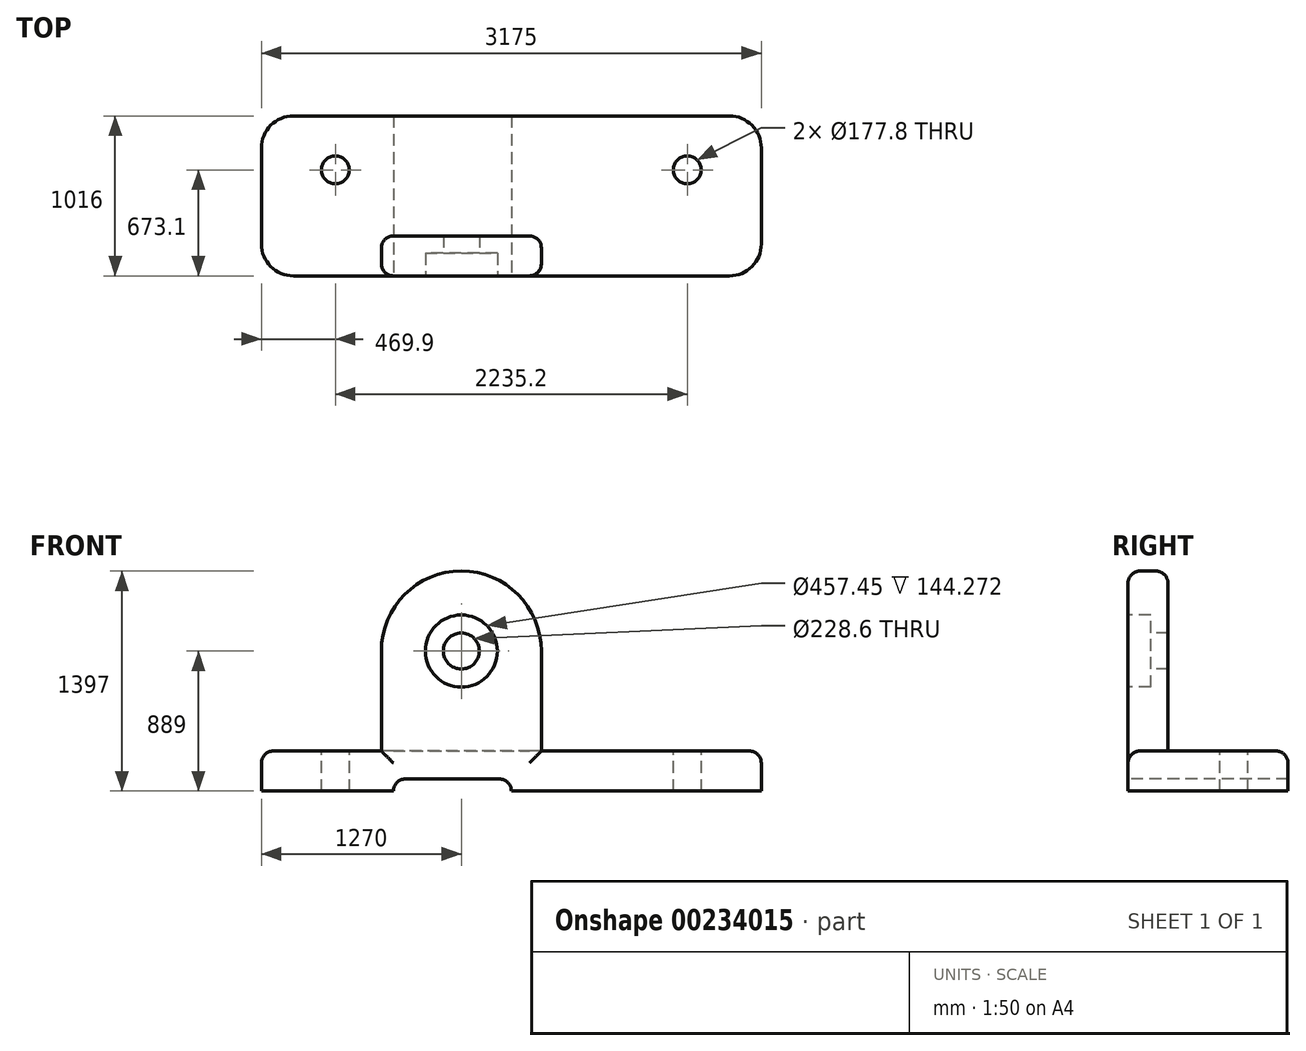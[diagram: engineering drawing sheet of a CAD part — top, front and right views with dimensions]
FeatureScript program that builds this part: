
annotation { "Feature Type Name" : "Feature", "Feature Type Description" : "" }
export const myFeature = defineFeature(function(context is Context, id is Id, definition is map)
    precondition{}
    {
        {
            var Q0;
            Q0=qCreatedBy(makeId("Top.planeOp"),FACE);
            var sketch = newSketch(context, id + "F0", { "sketchPlane" : qUnion([Q0])});
            skLineSegment(sketch, "E0.bottom", {"start": v(1587.5, -508) * mm, "end": v(-1587.5, -508) * mm});
            skLineSegment(sketch, "E0.top", {"start": v(1587.5, 508) * mm, "end": v(-1587.5, 508) * mm});
            skLineSegment(sketch, "E0.left", {"start": v(1587.5, -508) * mm, "end": v(1587.5, 508) * mm});
            skLineSegment(sketch, "E0.right", {"start": v(-1587.5, -508) * mm, "end": v(-1587.5, 508) * mm});
            skPoint(sketch, "E0.middle", {"position": v(0, 0) * mm});
            skSolve(sketch);
        }
        {
            var Q0;
            Q0=makeQuery(id+"F0.imprint","IMPRINT",FACE,{"disambiguationData":[TD([[makeQuery(id+"F0.imprint","IMPRINT",EDGE,{"derivedFrom":sQuery(id+"F0.wireOp",EDGE,"E0.bottom")}),-1.0]])]});
            extrude(context, id + "F1", {"entities" : qUnion([Q0]), "depth" : 254 * mm});
        }
        {
            var Q0;
            Q0=makeQuery(id+"F1.opExtrude","CAP_FACE",FACE,{"disambiguationData":[OSD([sQuery(id+"F0.wireOp",EDGE,"E0.bottom"),sQuery(id+"F0.wireOp",EDGE,"E0.top"),sQuery(id+"F0.wireOp",EDGE,"E0.left"),sQuery(id+"F0.wireOp",EDGE,"E0.right")])],"isStart":false});
            var sketch = newSketch(context, id + "F2", { "sketchPlane" : qUnion([Q0])});
            skLineSegment(sketch, "E1.bottom", {"start": v(-825.5, -508) * mm, "end": v(190.5, -508) * mm});
            skLineSegment(sketch, "E1.top", {"start": v(-825.5, -254) * mm, "end": v(190.5, -254) * mm});
            skLineSegment(sketch, "E1.left", {"start": v(-825.5, -508) * mm, "end": v(-825.5, -254) * mm});
            skLineSegment(sketch, "E1.right", {"start": v(190.5, -508) * mm, "end": v(190.5, -254) * mm});
            skSolve(sketch);
        }
        {
            var Q0;
            Q0=makeQuery(id+"F2.imprint","IMPRINT",FACE,{"disambiguationData":[TD([[makeQuery(id+"F2.imprint","IMPRINT",EDGE,{"derivedFrom":sQuery(id+"F2.wireOp",EDGE,"E1.bottom")}),-1.0]])]});
            extrude(context, id + "F3", {"entities" : qUnion([Q0]), "operationType" : NewBodyOperationType.ADD, "depth" : 1143 * mm});
        }
        {
            var Q0;
            Q0=makeQuery(id+"F3.opExtrude","CAP_EDGE",EDGE,{"disambiguationData":[OSD([sQuery(id+"F2.wireOp",EDGE,"E1.right")])],"isStart":false});
            var Q1;
            Q1=makeQuery(id+"F3.opExtrude","CAP_EDGE",EDGE,{"disambiguationData":[OSD([sQuery(id+"F2.wireOp",EDGE,"E1.left")])],"isStart":false});
            fillet(context, id + "F4", {"entities" : qUnion([Q0, Q1]), "radius" : 508 * mm, "tangentPropagation" : true, "allowEdgeOverflow" : false});
        }
        {
            var Q0;
            Q0=makeQuery(id+"F4.opFillet","BLEND_EDGE",EDGE,{"blendedFrom":[makeQuery(id+"F3.opExtrude","CAP_EDGE",EDGE,{"disambiguationData":[OSD([sQuery(id+"F2.wireOp",EDGE,"E1.left")])],"isStart":false}),makeQuery(id+"F3.boolean.opBoolean","MERGE",FACE,{"derivedFrom":[makeQuery(id+"F1.opExtrude","SWEPT_FACE",FACE,{"disambiguationData":[OSD([sQuery(id+"F0.wireOp",EDGE,"E0.bottom")])]}),makeQuery(id+"F3.opExtrude","SWEPT_FACE",FACE,{"disambiguationData":[OSD([sQuery(id+"F2.wireOp",EDGE,"E1.bottom")])]})]})],"blendedInto":[makeQuery(id+"F3.boolean.opBoolean","MERGE",FACE,{"derivedFrom":[makeQuery(id+"F1.opExtrude","SWEPT_FACE",FACE,{"disambiguationData":[OSD([sQuery(id+"F0.wireOp",EDGE,"E0.bottom")])]}),makeQuery(id+"F3.opExtrude","SWEPT_FACE",FACE,{"disambiguationData":[OSD([sQuery(id+"F2.wireOp",EDGE,"E1.bottom")])]})]})]});
            var Q1;
            {var subQ0=sQuery(id+"F0.wireOp",EDGE,"E0.left");var subQ1=sQuery(id+"F0.wireOp",EDGE,"E0.bottom");Q1=makeQuery(id+"F3.boolean.opBoolean","SPLIT",EDGE,{"disambiguationData":[TD([makeQuery(id+"F1.opExtrude","SWEPT_FACE",FACE,{"disambiguationData":[OSD([subQ0])]})])],"derivedFrom":makeQuery(id+"F1.opExtrude","CAP_EDGE",EDGE,{"disambiguationData":[OSD([subQ1])],"isStart":false})});}
            var Q2;
            {var subQ0=sQuery(id+"F0.wireOp",EDGE,"E0.right");var subQ1=sQuery(id+"F0.wireOp",EDGE,"E0.bottom");Q2=makeQuery(id+"F3.boolean.opBoolean","SPLIT",EDGE,{"disambiguationData":[TD([makeQuery(id+"F1.opExtrude","SWEPT_FACE",FACE,{"disambiguationData":[OSD([subQ0])]})])],"derivedFrom":makeQuery(id+"F1.opExtrude","CAP_EDGE",EDGE,{"disambiguationData":[OSD([subQ1])],"isStart":false})});}
            var Q3;
            Q3=makeQuery(id+"F1.opExtrude","CAP_EDGE",EDGE,{"disambiguationData":[OSD([sQuery(id+"F0.wireOp",EDGE,"E0.top")])],"isStart":false});
            var Q4;
            Q4=makeQuery(id+"F1.opExtrude","CAP_EDGE",EDGE,{"disambiguationData":[OSD([sQuery(id+"F0.wireOp",EDGE,"E0.left")])],"isStart":false});
            var Q5;
            Q5=makeQuery(id+"F1.opExtrude","CAP_EDGE",EDGE,{"disambiguationData":[OSD([sQuery(id+"F0.wireOp",EDGE,"E0.right")])],"isStart":false});
            var Q6;
            Q6=makeQuery(id+"F4.opFillet","BLEND_EDGE",EDGE,{"blendedFrom":[makeQuery(id+"F3.opExtrude","CAP_EDGE",EDGE,{"disambiguationData":[OSD([sQuery(id+"F2.wireOp",EDGE,"E1.left")])],"isStart":false}),makeQuery(id+"F3.opExtrude","SWEPT_FACE",FACE,{"disambiguationData":[OSD([sQuery(id+"F2.wireOp",EDGE,"E1.top")])]})],"blendedInto":[makeQuery(id+"F3.opExtrude","SWEPT_FACE",FACE,{"disambiguationData":[OSD([sQuery(id+"F2.wireOp",EDGE,"E1.top")])]})]});
            var Q7;
            Q7=makeQuery(id+"F3.opExtrude","CAP_EDGE",EDGE,{"disambiguationData":[OSD([sQuery(id+"F2.wireOp",EDGE,"E1.right")])],"isStart":true});
            fillet(context, id + "F5", {"entities" : qUnion([Q0, Q1, Q2, Q3, Q4, Q5, Q6, Q7]), "radius" : 76.2 * mm, "tangentPropagation" : true, "allowEdgeOverflow" : false});
        }
        {
            var Q0;
            Q0=makeQuery(id+"F3.boolean.opBoolean","MERGE",FACE,{"derivedFrom":[makeQuery(id+"F1.opExtrude","SWEPT_FACE",FACE,{"disambiguationData":[OSD([sQuery(id+"F0.wireOp",EDGE,"E0.bottom")])]}),makeQuery(id+"F3.opExtrude","SWEPT_FACE",FACE,{"disambiguationData":[OSD([sQuery(id+"F2.wireOp",EDGE,"E1.bottom")])]})]});
            var sketch = newSketch(context, id + "F6", { "sketchPlane" : qUnion([Q0])});
            skCircle(sketch, "E2", {"center": v(-317.5, 889) * mm, "radius": 228.73 * mm});
            skCircle(sketch, "E3", {"center": v(-317.5, 889) * mm, "radius": 114.3 * mm});
            skSolve(sketch);
        }
        {
            var Q0;
            Q0=makeQuery(id+"F6.imprint","IMPRINT",FACE,{"disambiguationData":[TD([[makeQuery(id+"F6.imprint","IMPRINT",EDGE,{"derivedFrom":sQuery(id+"F6.wireOp",EDGE,"E2")}),1.0]])]});
            extrude(context, id + "F7", {"entities" : qUnion([Q0]), "operationType" : NewBodyOperationType.REMOVE, "oppositeDirection" : true, "depth" : 144.27 * mm});
        }
        {
            var Q0;
            Q0=makeQuery(id+"F7.boolean.opBoolean","SPLIT",FACE,{"disambiguationData":[TD([makeQuery(id+"F7.opExtrude","SWEPT_FACE",FACE,{"disambiguationData":[OSD([sQuery(id+"F6.wireOp",EDGE,"E3")])]})])],"derivedFrom":makeQuery(id+"F3.boolean.opBoolean","MERGE",FACE,{"derivedFrom":[makeQuery(id+"F1.opExtrude","SWEPT_FACE",FACE,{"disambiguationData":[OSD([sQuery(id+"F0.wireOp",EDGE,"E0.bottom")])]}),makeQuery(id+"F3.opExtrude","SWEPT_FACE",FACE,{"disambiguationData":[OSD([sQuery(id+"F2.wireOp",EDGE,"E1.bottom")])]})]})});
            extrude(context, id + "F8", {"entities" : qUnion([Q0]), "operationType" : NewBodyOperationType.REMOVE, "oppositeDirection" : true, "depth" : 817.88 * mm});
        }
        {
            var Q0;
            {var subQ0=sQuery(id+"F0.wireOp",EDGE,"E0.left");var subQ1=sQuery(id+"F0.wireOp",EDGE,"E0.bottom");Q0=makeQuery(id+"F5.opFillet","BLEND_EDGE",EDGE,{"blendedFrom":[makeQuery(id+"F1.opExtrude","CAP_EDGE",EDGE,{"disambiguationData":[OSD([subQ0])],"isStart":false}),makeQuery(id+"F3.boolean.opBoolean","SPLIT",EDGE,{"disambiguationData":[TD([makeQuery(id+"F1.opExtrude","SWEPT_FACE",FACE,{"disambiguationData":[OSD([subQ0])]})])],"derivedFrom":makeQuery(id+"F1.opExtrude","CAP_EDGE",EDGE,{"disambiguationData":[OSD([subQ1])],"isStart":false})})],"blendedInto":[]});}
            var Q1;
            Q1=makeQuery(id+"F5.opFillet","BLEND_EDGE",EDGE,{"blendedFrom":[makeQuery(id+"F1.opExtrude","CAP_EDGE",EDGE,{"disambiguationData":[OSD([sQuery(id+"F0.wireOp",EDGE,"E0.top")])],"isStart":false}),makeQuery(id+"F1.opExtrude","CAP_EDGE",EDGE,{"disambiguationData":[OSD([sQuery(id+"F0.wireOp",EDGE,"E0.left")])],"isStart":false})],"blendedInto":[]});
            var Q2;
            {var subQ0=sQuery(id+"F0.wireOp",EDGE,"E0.right");var subQ1=sQuery(id+"F0.wireOp",EDGE,"E0.bottom");Q2=makeQuery(id+"F5.opFillet","BLEND_EDGE",EDGE,{"blendedFrom":[makeQuery(id+"F1.opExtrude","CAP_EDGE",EDGE,{"disambiguationData":[OSD([subQ0])],"isStart":false}),makeQuery(id+"F3.boolean.opBoolean","SPLIT",EDGE,{"disambiguationData":[TD([makeQuery(id+"F1.opExtrude","SWEPT_FACE",FACE,{"disambiguationData":[OSD([subQ0])]})])],"derivedFrom":makeQuery(id+"F1.opExtrude","CAP_EDGE",EDGE,{"disambiguationData":[OSD([subQ1])],"isStart":false})})],"blendedInto":[]});}
            var Q3;
            Q3=makeQuery(id+"F5.opFillet","BLEND_EDGE",EDGE,{"blendedFrom":[makeQuery(id+"F1.opExtrude","CAP_EDGE",EDGE,{"disambiguationData":[OSD([sQuery(id+"F0.wireOp",EDGE,"E0.top")])],"isStart":false}),makeQuery(id+"F1.opExtrude","CAP_EDGE",EDGE,{"disambiguationData":[OSD([sQuery(id+"F0.wireOp",EDGE,"E0.right")])],"isStart":false})],"blendedInto":[]});
            fillet(context, id + "F9", {"entities" : qUnion([Q0, Q1, Q2, Q3]), "radius" : 203.2 * mm, "tangentPropagation" : true, "allowEdgeOverflow" : false});
        }
        {
            var Q0;
            Q0=makeQuery(id+"F1.opExtrude","CAP_FACE",FACE,{"disambiguationData":[OSD([sQuery(id+"F0.wireOp",EDGE,"E0.bottom"),sQuery(id+"F0.wireOp",EDGE,"E0.top"),sQuery(id+"F0.wireOp",EDGE,"E0.left"),sQuery(id+"F0.wireOp",EDGE,"E0.right")])],"isStart":false});
            var sketch = newSketch(context, id + "F10", { "sketchPlane" : qUnion([Q0])});
            skCircle(sketch, "E4", {"center": v(1117.6, 165.1) * mm, "radius": 88.9 * mm});
            skCircle(sketch, "E5", {"center": v(-1117.6, 165.1) * mm, "radius": 88.9 * mm});
            skSolve(sketch);
        }
        {
            var Q0;
            Q0 = qSketchRegion(id + "F10", true);
            extrude(context, id + "F11", {"entities" : qUnion([Q0]), "operationType" : NewBodyOperationType.REMOVE, "oppositeDirection" : true, "depth" : 792.48 * mm});
        }
        {
            var Q0;
            {var subQ2=sQuery(id+"F2.wireOp",EDGE,"E1.bottom");var subQ3=makeQuery(id+"F3.opExtrude","SWEPT_FACE",FACE,{"disambiguationData":[OSD([subQ2])]});var subQ4=sQuery(id+"F0.wireOp",EDGE,"E0.left");var subQ6=sQuery(id+"F0.wireOp",EDGE,"E0.bottom");var subQ8=makeQuery(id+"F1.opExtrude","SWEPT_FACE",FACE,{"disambiguationData":[OSD([subQ6])]});var subQ11=makeQuery(id+"F1.opExtrude","SWEPT_FACE",FACE,{"disambiguationData":[OSD([subQ4])]});var subQ13=makeQuery(id+"F3.boolean.opBoolean","MERGE",FACE,{"derivedFrom":[subQ8,subQ3]});Q0=makeQuery(id+"F7.boolean.opBoolean","SPLIT",FACE,{"disambiguationData":[TD([subQ11])],"derivedFrom":subQ13});}
            var sketch = newSketch(context, id + "F12", { "sketchPlane" : qUnion([Q0])});
            skLineSegment(sketch, "E6", {"start": v(-749.3, 0) * mm, "end": v(-749.3, 0) * mm});
            skLineSegment(sketch, "E7", {"start": v(-673.1, 76.2) * mm, "end": v(-76.2, 76.2) * mm});
            skLineSegment(sketch, "E8", {"start": v(0, 0) * mm, "end": v(0, 0) * mm});
            skLineSegment(sketch, "E9", {"start": v(0, 0) * mm, "end": v(-749.3, 0) * mm});
            skPoint(sketch, "E10.visualSharp", {"position": v(0, 76.2) * mm});
            skArc(sketch, "E10.filletArc", {"start": v(0, 0) * mm, "mid": v(-22.32, 53.88) * mm, "end": v(-76.2, 76.2) * mm});
            skPoint(sketch, "E11.visualSharp", {"position": v(-749.3, 76.2) * mm});
            skArc(sketch, "E11.filletArc", {"start": v(-673.1, 76.2) * mm, "mid": v(-726.98, 53.88) * mm, "end": v(-749.3, 0) * mm});
            skSolve(sketch);
        }
        {
            var Q0;
            Q0=makeQuery(id+"F12.imprint","IMPRINT",FACE,{"disambiguationData":[TD([[makeQuery(id+"F12.imprint","IMPRINT",EDGE,{"derivedFrom":sQuery(id+"F12.wireOp",EDGE,"E7")}),-1.0]])]});
            extrude(context, id + "F13", {"entities" : qUnion([Q0]), "operationType" : NewBodyOperationType.REMOVE, "oppositeDirection" : true, "depth" : 1478.28 * mm});
        }
    });
